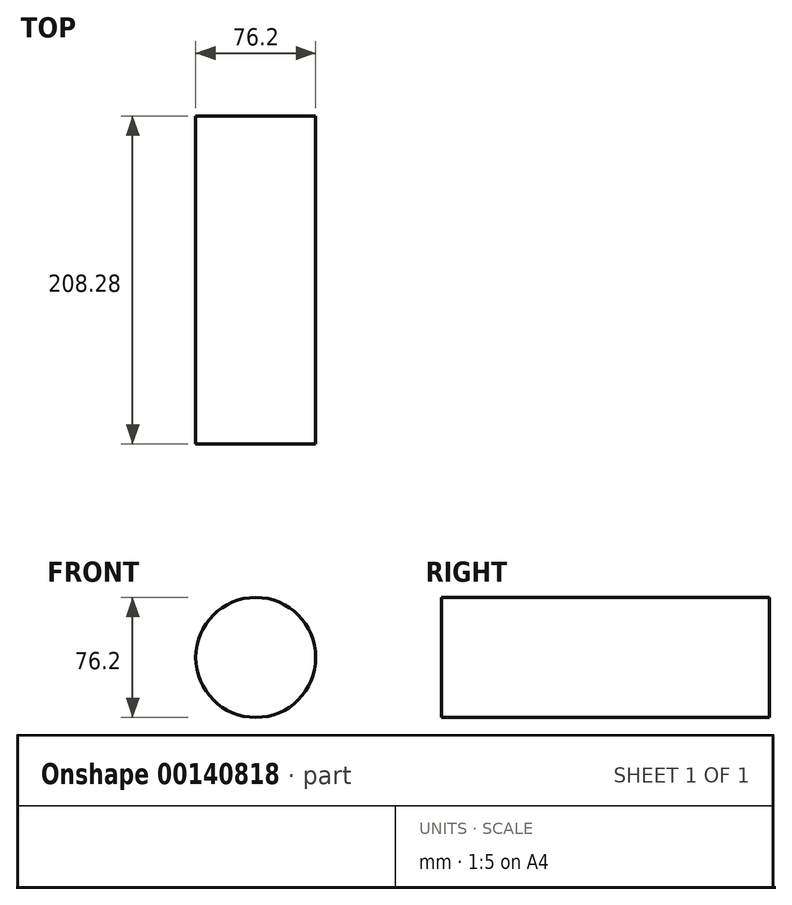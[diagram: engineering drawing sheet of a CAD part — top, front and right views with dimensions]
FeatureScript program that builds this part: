
annotation { "Feature Type Name" : "Feature", "Feature Type Description" : "" }
export const myFeature = defineFeature(function(context is Context, id is Id, definition is map)
    precondition{}
    {
        {
            var Q0;
            Q0=qCreatedBy(makeId("Front.planeOp"),FACE);
            var sketch = newSketch(context, id + "F0", { "sketchPlane" : qUnion([Q0])});
            skCircle(sketch, "E0", {"center": v(6.35, 0) * mm, "radius": 38.1 * mm});
            skSolve(sketch);
        }
        {
            var Q0;
            Q0=makeQuery(id+"F0.imprint","IMPRINT",FACE,{"disambiguationData":[TD([[makeQuery(id+"F0.imprint","IMPRINT",EDGE,{"derivedFrom":sQuery(id+"F0.wireOp",EDGE,"E0")}),1.0]])]});
            extrude(context, id + "F1", {"entities" : qUnion([Q0]), "endBound" : BoundingType.SYMMETRIC, "depth" : 208.28 * mm});
        }
    });
